# Revit family: Lighting_Outside_Nordlux_Arki-35-Outdoor-Wall
name_source: partatom
category: Lighting Fixtures
revit_build: Autodesk Revit 2018 (Build: 20190510_1515(x64)
units: mm (PartAtom-declared; Revit-internal decimal feet)

## family parameters
Cut with Voids When Loaded = No
Host = Face
Light Source = Yes
OmniClass Number = 23.35.47.11
OmniClass Title = Lighting Fixtures
Part Type = Normal
Room Calculation Point = No
Round Connector Dimension = Use Diameter
Shared = No

## types (2) — shared parameters
Apparent Load = 7 VA
BIMobject category = Outside
Beam angle = 100.90°
CQS = 81.4
CRI / Ra = 81
Color Filter = 16777215
Default Elevation = 1219 mm
Description = The Arki series by Danish designer Bønnelycke MDD is characterised by its beautiful dome-like shade and minimalist, clean lines inspired by the classic architect lamp. The oversize shade adds a grandiose and spectacular quality to your house façade. Arki beautifully balances simplicity with sophistication while emitting the perfect light for your entrance, driveway, terrace or other outdoor space.
Design country = Denmark
Dimming Lamp Color Temperature Shift = <None>
Edition number = 1
Emit Shape Visible in Rendering = No
Emit from Circle Diameter = 60 mm  [stored 0.19685 ft]
Flicker frequency = 99 Hz
IFC Classification = Light Fixture
Installation instructions = https://asset.productmarketingcloud.com
Lens material = Nordlux - Glass - Glass transparent
Manufacturer = Nordlux
Manufacturer country = China
Manufacturer name = Nordlux
Material main = Metal
Material secondary = Plastic
Model = Arki 35
NominalVoltage = 230 V
OmniClass Code = 23-35 47 11
OmniClass Description = Lighting Fixtures
Peak [cd] = 109
Photometric Web File = Arki 35 Outdoor Galv..ies
Power factor = 0.53
Product Guid = 73a8bf63-f5a7-4e14-be04-49d39f7d0b16
Product SKU = Arki-35-Outdoor-Wall
Product data url = https://bimobject.com
Product family = Lighting
Product group = Wall
Product name = Arki 35 Outdoor Wall
Product url = https://nordlux.com
QR code = https://bimobject.com
TM30 Rf = 85
TM30 Rg = 93.8
Tilt Angle = 90.00°
URL = www.nordlux.com
Weight Net (Kg) = 2.67

## per-type parameters (varying)
| type | Body material | EANNumber |
| ART - (2118111003) Finish colour - (Black) | Nordlux - Metal - Black | 2118111003 |
| ART - (2118111031) Finish colour - (Galvanized) | Nordlux - Metal - Galvanized steel | 2118111031 |

note: [stored X ft] marks values corroborated as IEEE doubles in the binary element streams (Revit-internal decimal feet)

## geometry (parser evidence)
native form markers: Sweep x2
no freeform markers — native parametric forms only
